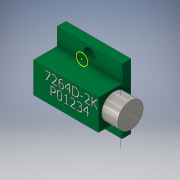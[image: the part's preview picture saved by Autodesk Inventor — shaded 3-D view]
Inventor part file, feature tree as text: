
AUTODESK INVENTOR PART (.ipt)
format: ipt  version: 2016 (Build 200138000, 138)  size: 559,616 bytes
history: native  units: in
note: dims shown in document units (in); Inventor stores cm internally (conversion verified against a paired STEP export)
features: sketch x4, extrude x3, other x3, emboss x1, plane x1
ambient origin geometry x8: Origin, YZ Plane, XZ Plane, XY Plane, X Axis, Y Axis, Z Axis, Center Point
bodies: Solid1 (feature_tree)
feature tree (12):
  extrude  "Extrusion1"  Depth=0.4in
  extrude  "Extrusion2"  Depth=0.05in
  extrude  "Extrusion3"  Depth=0.188in
  emboss  "Emboss1"
  plane  "Work Plane1"
  other  "Center of Seismic Mass"
  sketch  "Sketch1"  dims[d1=0.4in d2=0.4in]
  sketch  "Sketch2"  dims[d3=0.071in d4=0.05in]
  sketch  "Sketch3"  dims[d5=0.055in d6=0.0in d7=0.188in]
  sketch  "Sketch4"  dims[d8=0.145in d9=0.0in d10=0.156in d11=0.103in d12=0.1in d13=0.0in d14=0.001in d15=0.0in d19=0.24in]
  other  "Work Axis2"
  other  "Work Point2"
